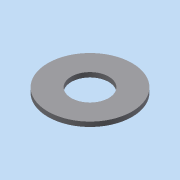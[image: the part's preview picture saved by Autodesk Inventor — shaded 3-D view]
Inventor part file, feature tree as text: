
AUTODESK INVENTOR PART (.ipt)
format: ipt  version: 2015 (Build 190159000, 159)  size: 73,216 bytes
history: native  units: mm
features: extrude x1, sketch x1
ambient origin geometry x8: Origin, YZ Plane, XZ Plane, XY Plane, X Axis, Y Axis, Z Axis, Center Point
bodies: Solid1 (feature_tree)
feature tree (2):
  extrude  "Extrusion1"  Depth=0.5mm
  sketch  "Sketch1"  dims[d0=4.0mm d1=9.0mm d2=0.5mm d3=0.0mm]
